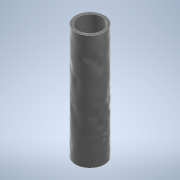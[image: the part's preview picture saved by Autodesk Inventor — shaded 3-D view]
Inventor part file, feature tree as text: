
AUTODESK INVENTOR PART (.ipt)
format: ipt  version: 2022 (Build 260153000, 153)  size: 102,400 bytes
history: native  units: mm
features: extrude x1, sketch x1
ambient origin geometry x8: Origin, YZ Plane, XZ Plane, XY Plane, X Axis, Y Axis, Z Axis, Center Point
bodies: Solid1 (feature_tree)
feature tree (2):
  extrude  "Extrusion1"  Depth=23.0mm
  sketch  "Sketch1"  dims[d0=4.8mm d1=5.8mm d2=23.0mm d3=0.0mm]
